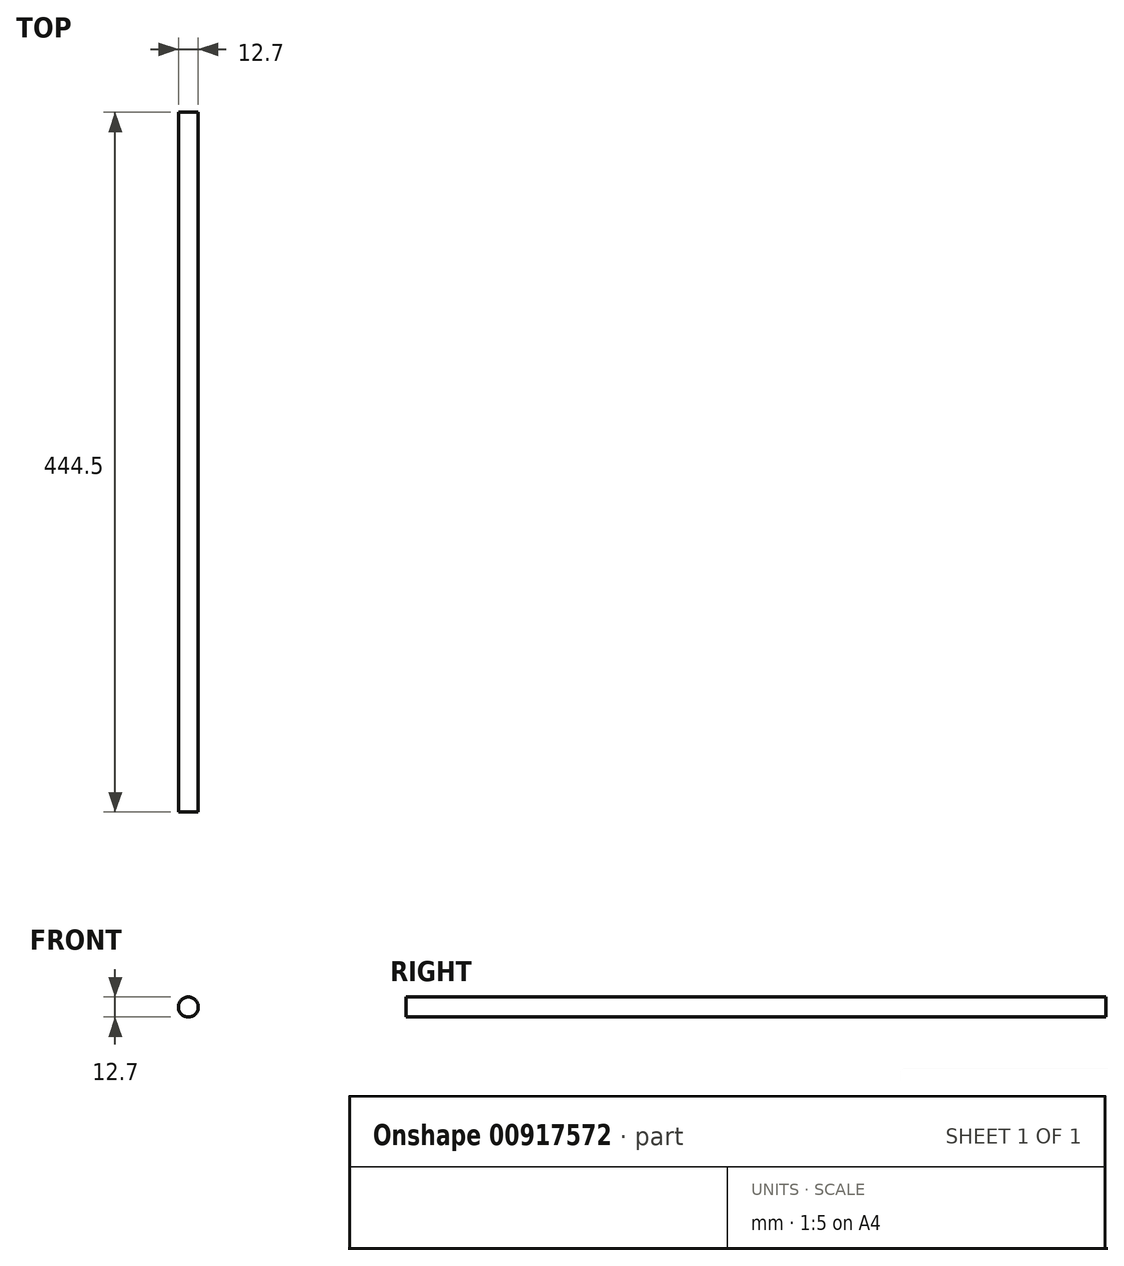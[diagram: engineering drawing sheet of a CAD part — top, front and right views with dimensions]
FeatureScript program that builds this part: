
annotation { "Feature Type Name" : "Feature", "Feature Type Description" : "" }
export const myFeature = defineFeature(function(context is Context, id is Id, definition is map)
    precondition{}
    {
        {
            var Q0;
            Q0=qCreatedBy(makeId("Front.planeOp"),FACE);
            var sketch = newSketch(context, id + "F0", { "sketchPlane" : qUnion([Q0])});
            skCircle(sketch, "E0", {"center": v(0, 0) * mm, "radius": 6.35 * mm});
            skSolve(sketch);
        }
        {
            var Q0;
            Q0=makeQuery(id+"F0.imprint","IMPRINT",FACE,{"disambiguationData":[TD([[makeQuery(id+"F0.imprint","IMPRINT",EDGE,{"derivedFrom":sQuery(id+"F0.wireOp",EDGE,"E0")}),1.0]])]});
            extrude(context, id + "F1", {"entities" : qUnion([Q0]), "depth" : 444.5 * mm, "offsetDistance" : 25.4 * mm});
        }
    });
